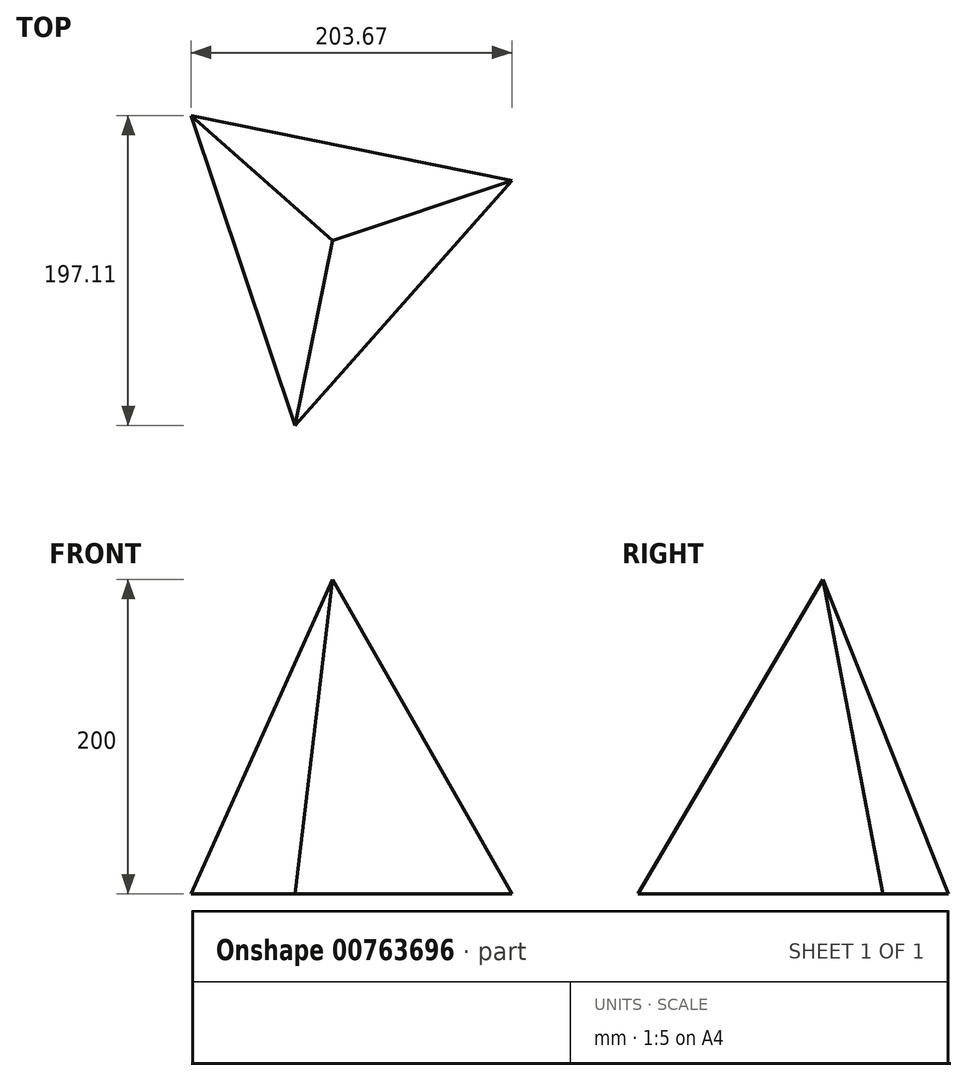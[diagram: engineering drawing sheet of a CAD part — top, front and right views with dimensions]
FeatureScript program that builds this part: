
annotation { "Feature Type Name" : "Feature", "Feature Type Description" : "" }
export const myFeature = defineFeature(function(context is Context, id is Id, definition is map)
    precondition{}
    {
        {
            var Q0;
            Q0=qCreatedBy(makeId("Top.planeOp"),FACE);
            var sketch = newSketch(context, id + "F0", { "sketchPlane" : qUnion([Q0])});
            skCircle(sketch, "E0.cCircle", {"center": v(0, 0) * mm, "radius": 120 * mm, "construction": true});
            skLineSegment(sketch, "E0.0", {"start": v(-89.87, 79.52) * mm, "end": v(113.8, 38.06) * mm});
            skLineSegment(sketch, "E0.1", {"start": v(113.8, 38.06) * mm, "end": v(-23.94, -117.59) * mm});
            skLineSegment(sketch, "E0.2", {"start": v(-23.94, -117.59) * mm, "end": v(-89.87, 79.52) * mm});
            skSolve(sketch);
        }
        {
            var Q0;
            Q0=qCreatedBy(makeId("Top.planeOp"),FACE);
            cPlane(context, id + "F1", {"entities" : qUnion([Q0]), "cplaneType" : CPlaneType.OFFSET, "offset" : 200 * mm, "width" : 150 * mm, "height" : 150 * mm});
        }
        {
            var Q0;
            Q0=qCreatedBy(id+"F1.planeOp",FACE);
            var sketch = newSketch(context, id + "F2", { "sketchPlane" : qUnion([Q0])});
            skPoint(sketch, "E1.0", {"position": v(0, 0) * mm});
            skSolve(sketch);
        }
        {
            var Q0;
            Q0=makeQuery(id+"F0.imprint","IMPRINT",FACE,{"disambiguationData":[TD([[makeQuery(id+"F0.imprint","IMPRINT",EDGE,{"derivedFrom":sQuery(id+"F0.wireOp",EDGE,"E0.0")}),-1.0]])]});
            var Q1;
            Q1=sQuery(id+"F2.wireOp",VERTEX,"E1.0");
            loft(context, id + "F3", {"sheetProfilesArray" : [{ "sheetProfileEntities" : qUnion([Q0]) }, { "sheetProfileEntities" : qUnion([Q1]) }]});
        }
    });
